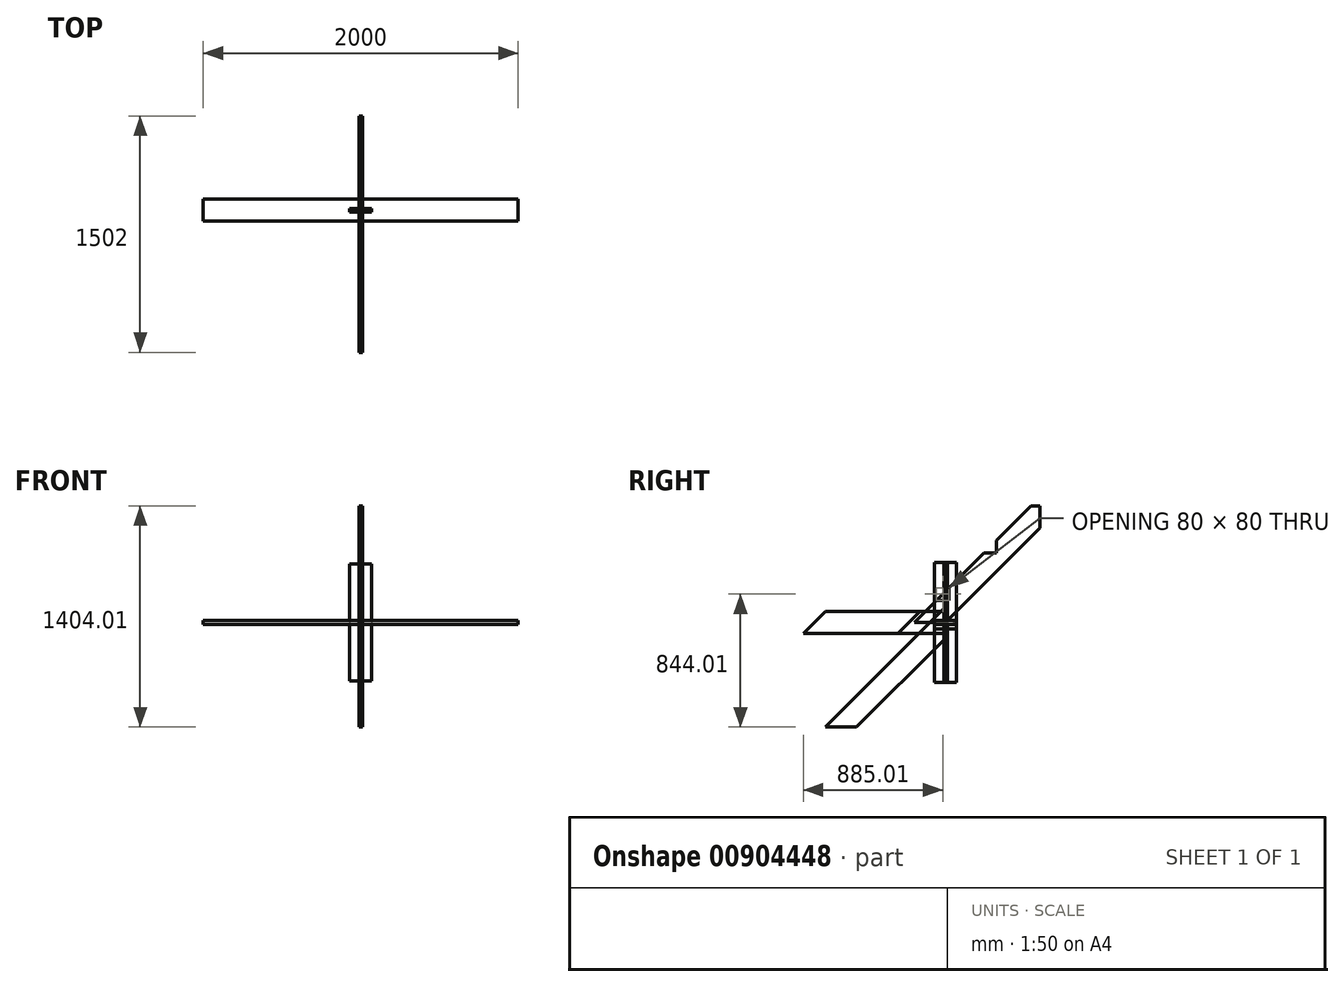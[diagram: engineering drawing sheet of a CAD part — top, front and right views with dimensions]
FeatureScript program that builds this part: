
annotation { "Feature Type Name" : "Feature", "Feature Type Description" : "" }
export const myFeature = defineFeature(function(context is Context, id is Id, definition is map)
    precondition{}
    {
        {
            var Q0;
            Q0=qCreatedBy(makeId("Right.planeOp"),FACE);
            var sketch = newSketch(context, id + "F0", { "sketchPlane" : qUnion([Q0])});
            skLineSegment(sketch, "E0.bottom", {"start": v(-70, 11.5) * mm, "end": v(70, 11.5) * mm});
            skLineSegment(sketch, "E0.top", {"start": v(-70, -11.5) * mm, "end": v(70, -11.5) * mm});
            skLineSegment(sketch, "E0.left", {"start": v(-70, 11.5) * mm, "end": v(-70, -11.5) * mm});
            skLineSegment(sketch, "E0.right", {"start": v(70, 11.5) * mm, "end": v(70, -11.5) * mm});
            skSolve(sketch);
        }
        {
            var Q0;
            Q0 = qSketchRegion(id + "F0", true);
            extrude(context, id + "F1", {"entities" : qUnion([Q0]), "endBound" : BoundingType.SYMMETRIC, "depth" : 2000 * mm, "offsetDistance" : 25 * mm});
        }
        {
            var Q0;
            Q0=qCreatedBy(makeId("Top.planeOp"),FACE);
            var sketch = newSketch(context, id + "F2", { "sketchPlane" : qUnion([Q0])});
            skLineSegment(sketch, "E1.bottom", {"start": v(-11.5, -70) * mm, "end": v(11.5, -70) * mm});
            skLineSegment(sketch, "E1.top", {"start": v(-11.5, 70) * mm, "end": v(11.5, 70) * mm});
            skLineSegment(sketch, "E1.left", {"start": v(-11.5, -70) * mm, "end": v(-11.5, 70) * mm});
            skLineSegment(sketch, "E1.right", {"start": v(11.5, -70) * mm, "end": v(11.5, 70) * mm});
            skSolve(sketch);
        }
        {
            var Q0;
            Q0 = qSketchRegion(id + "F2", true);
            extrude(context, id + "F3", {"entities" : qUnion([Q0]), "endBound" : BoundingType.SYMMETRIC, "depth" : 763 * mm, "offsetDistance" : 25 * mm});
        }
        {
            var Q0;
            Q0=qCreatedBy(makeId("Right.planeOp"),FACE);
            var sketch = newSketch(context, id + "F4", { "sketchPlane" : qUnion([Q0])});
            skLineSegment(sketch, "E2", {"start": v(0, 99) * mm, "end": v(0, -99) * mm});
            skLineSegment(sketch, "E3", {"start": v(0, -99) * mm, "end": v(-565.01, -664) * mm});
            skLineSegment(sketch, "E4", {"start": v(-763, -664) * mm, "end": v(0, 99) * mm});
            skLineSegment(sketch, "E5", {"start": v(-763, -664) * mm, "end": v(-565.01, -664) * mm});
            skSolve(sketch);
        }
        {
            var Q0;
            Q0 = qSketchRegion(id + "F4", true);
            extrude(context, id + "F5", {"entities" : qUnion([Q0]), "endBound" : BoundingType.SYMMETRIC, "depth" : 23 * mm, "offsetDistance" : 25 * mm});
        }
        {
            var Q0;
            Q0=qCreatedBy(makeId("Right.planeOp"),FACE);
            var sketch = newSketch(context, id + "F6", { "sketchPlane" : qUnion([Q0])});
            skLineSegment(sketch, "E6", {"start": v(0, 70) * mm, "end": v(0, -70) * mm});
            skLineSegment(sketch, "E7", {"start": v(0, -70) * mm, "end": v(-303, -70) * mm});
            skLineSegment(sketch, "E8", {"start": v(-303, -70) * mm, "end": v(-163, 70) * mm});
            skLineSegment(sketch, "E9", {"start": v(-163, 70) * mm, "end": v(0, 70) * mm});
            skSolve(sketch);
        }
        {
            var Q0;
            Q0 = qSketchRegion(id + "F6", true);
            extrude(context, id + "F7", {"entities" : qUnion([Q0]), "endBound" : BoundingType.SYMMETRIC, "depth" : 23 * mm, "offsetDistance" : 25 * mm});
        }
        {
            var Q0;
            Q0=qCreatedBy(makeId("Right.planeOp"),FACE);
            var sketch = newSketch(context, id + "F8", { "sketchPlane" : qUnion([Q0])});
            skLineSegment(sketch, "E10", {"start": v(0, 70) * mm, "end": v(0, -70) * mm});
            skLineSegment(sketch, "E11", {"start": v(0, -70) * mm, "end": v(-903, -70) * mm});
            skLineSegment(sketch, "E12", {"start": v(-903, -70) * mm, "end": v(-763, 70) * mm});
            skLineSegment(sketch, "E13", {"start": v(-763, 70) * mm, "end": v(0, 70) * mm});
            skSolve(sketch);
        }
        {
            var Q0;
            Q0 = qSketchRegion(id + "F8", true);
            extrude(context, id + "F9", {"entities" : qUnion([Q0]), "endBound" : BoundingType.SYMMETRIC, "depth" : 23 * mm, "offsetDistance" : 25 * mm});
        }
        {
            var Q0;
            Q0=qCreatedBy(makeId("Front.planeOp"),FACE);
            var sketch = newSketch(context, id + "F10", { "sketchPlane" : qUnion([Q0])});
            skLineSegment(sketch, "E14", {"start": v(-70, 0) * mm, "end": v(70, 0) * mm, "construction": true});
            skLineSegment(sketch, "E15", {"start": v(0, 370) * mm, "end": v(0, -370) * mm, "construction": true});
            skLineSegment(sketch, "E16", {"start": v(-70, 370) * mm, "end": v(70, 370) * mm});
            skLineSegment(sketch, "E17", {"start": v(70, 370) * mm, "end": v(70, -370) * mm});
            skLineSegment(sketch, "E18", {"start": v(70, -370) * mm, "end": v(-70, -370) * mm});
            skLineSegment(sketch, "E19", {"start": v(-70, 370) * mm, "end": v(-70, -370) * mm});
            skSolve(sketch);
        }
        {
            var Q0;
            Q0 = qSketchRegion(id + "F10", true);
            extrude(context, id + "F11", {"entities" : qUnion([Q0]), "endBound" : BoundingType.SYMMETRIC, "depth" : 23 * mm, "offsetDistance" : 25 * mm});
        }
        {
            var Q0;
            Q0=qCreatedBy(makeId("Right.planeOp"),FACE);
            var sketch = newSketch(context, id + "F12", { "sketchPlane" : qUnion([Q0])});
            skLineSegment(sketch, "E20", {"start": v(0, 0) * mm, "end": v(-197.99, 0) * mm});
            skLineSegment(sketch, "E21", {"start": v(-197.99, 0) * mm, "end": v(542.01, 740) * mm});
            skLineSegment(sketch, "E22", {"start": v(542.01, 740) * mm, "end": v(740, 740) * mm});
            skLineSegment(sketch, "E23", {"start": v(740, 740) * mm, "end": v(0, 0) * mm});
            skSolve(sketch);
        }
        {
            var Q0;
            Q0 = qSketchRegion(id + "F12", true);
            extrude(context, id + "F13", {"entities" : qUnion([Q0]), "endBound" : BoundingType.SYMMETRIC, "depth" : 23 * mm, "offsetDistance" : 25 * mm});
        }
        {
            var Q0;
            Q0=makeQuery(id+"F13.opExtrude","CAP_FACE",FACE,{"disambiguationData":[OSD([sQuery(id+"F12.wireOp",EDGE,"E20"),sQuery(id+"F12.wireOp",EDGE,"E21"),sQuery(id+"F12.wireOp",EDGE,"E22"),sQuery(id+"F12.wireOp",EDGE,"E23")])],"isStart":false});
            var sketch = newSketch(context, id + "F14", { "sketchPlane" : qUnion([Q0])});
            skLineSegment(sketch, "E24", {"start": v(-57.99, 140) * mm, "end": v(22.01, 140) * mm});
            skLineSegment(sketch, "E25", {"start": v(22.01, 140) * mm, "end": v(22.01, 220) * mm});
            skLineSegment(sketch, "E26", {"start": v(22.01, 220) * mm, "end": v(-57.99, 140) * mm});
            skSolve(sketch);
        }
        {
            var Q0;
            Q0 = qSketchRegion(id + "F14", true);
            extrude(context, id + "F15", {"entities" : qUnion([Q0]), "operationType" : NewBodyOperationType.REMOVE, "endBound" : BoundingType.UP_TO_NEXT, "oppositeDirection" : true, "depth" : 25 * mm, "offsetDistance" : 25 * mm});
        }
        {
            var Q0;
            Q0=makeQuery(id+"F13.opExtrude","CAP_FACE",FACE,{"disambiguationData":[OSD([sQuery(id+"F12.wireOp",EDGE,"E20"),sQuery(id+"F12.wireOp",EDGE,"E21"),sQuery(id+"F12.wireOp",EDGE,"E22"),sQuery(id+"F12.wireOp",EDGE,"E23")])],"isStart":false});
            var sketch = newSketch(context, id + "F16", { "sketchPlane" : qUnion([Q0])});
            skLineSegment(sketch, "E27", {"start": v(242.01, 440) * mm, "end": v(322.01, 440) * mm});
            skLineSegment(sketch, "E28", {"start": v(322.01, 440) * mm, "end": v(322.01, 520) * mm});
            skLineSegment(sketch, "E29", {"start": v(322.01, 520) * mm, "end": v(242.01, 440) * mm});
            skSolve(sketch);
        }
        {
            var Q0;
            Q0 = qSketchRegion(id + "F16", true);
            extrude(context, id + "F17", {"entities" : qUnion([Q0]), "operationType" : NewBodyOperationType.REMOVE, "endBound" : BoundingType.UP_TO_NEXT, "oppositeDirection" : true, "depth" : 25 * mm, "offsetDistance" : 25 * mm});
        }
        {
            var Q0;
            Q0=makeQuery(id+"F13.opExtrude","CAP_FACE",FACE,{"disambiguationData":[OSD([sQuery(id+"F12.wireOp",EDGE,"E20"),sQuery(id+"F12.wireOp",EDGE,"E21"),sQuery(id+"F12.wireOp",EDGE,"E22"),sQuery(id+"F12.wireOp",EDGE,"E23")])],"isStart":false});
            var sketch = newSketch(context, id + "F18", { "sketchPlane" : qUnion([Q0])});
            skLineSegment(sketch, "E30", {"start": v(599, 740) * mm, "end": v(599, 599) * mm});
            skLineSegment(sketch, "E31", {"start": v(599, 599) * mm, "end": v(740, 740) * mm});
            skLineSegment(sketch, "E32", {"start": v(740, 740) * mm, "end": v(599, 740) * mm});
            skSolve(sketch);
        }
        {
            var Q0;
            Q0 = qSketchRegion(id + "F18", true);
            extrude(context, id + "F19", {"entities" : qUnion([Q0]), "operationType" : NewBodyOperationType.REMOVE, "endBound" : BoundingType.UP_TO_NEXT, "oppositeDirection" : true, "depth" : 25 * mm, "offsetDistance" : 25 * mm});
        }
        {
            var Q0;
            Q0=qCreatedBy(makeId("Right.planeOp"),FACE);
            var sketch = newSketch(context, id + "F20", { "sketchPlane" : qUnion([Q0])});
            skLineSegment(sketch, "E33.bottom", {"start": v(-70, 0) * mm, "end": v(70, 0) * mm});
            skLineSegment(sketch, "E33.top", {"start": v(-70, -40) * mm, "end": v(70, -40) * mm});
            skLineSegment(sketch, "E33.left", {"start": v(-70, 0) * mm, "end": v(-70, -40) * mm});
            skLineSegment(sketch, "E33.right", {"start": v(70, 0) * mm, "end": v(70, -40) * mm});
            skSolve(sketch);
        }
        {
            var Q0;
            Q0 = qSketchRegion(id + "F20", true);
            extrude(context, id + "F21", {"entities" : qUnion([Q0]), "endBound" : BoundingType.SYMMETRIC, "depth" : 23 * mm, "offsetDistance" : 25 * mm});
        }
    });
